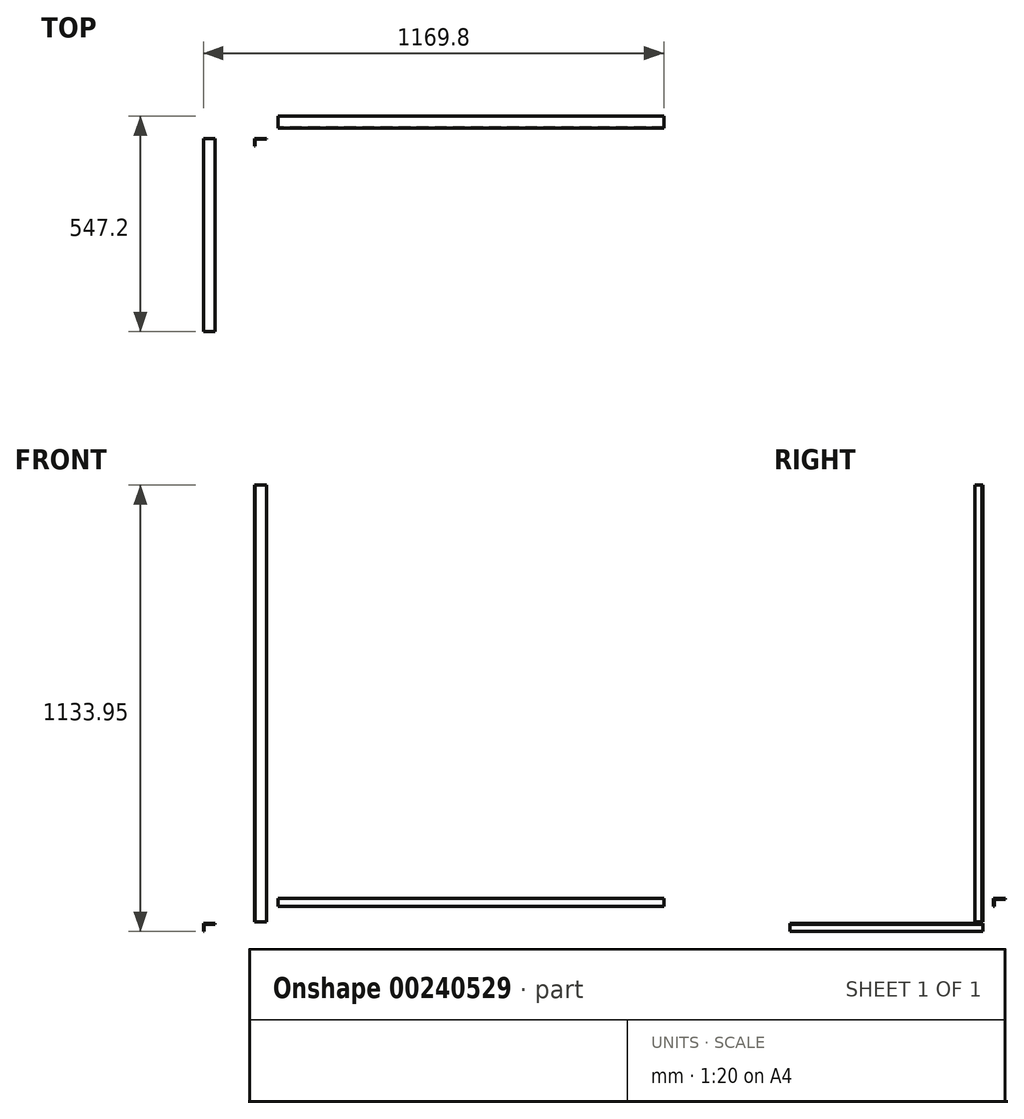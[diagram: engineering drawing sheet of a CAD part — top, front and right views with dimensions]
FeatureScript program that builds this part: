
annotation { "Feature Type Name" : "Feature", "Feature Type Description" : "" }
export const myFeature = defineFeature(function(context is Context, id is Id, definition is map)
    precondition{}
    {
        {
            var Q0;
            Q0=qCreatedBy(makeId("Front.planeOp"),FACE);
            var sketch = newSketch(context, id + "F0", { "sketchPlane" : qUnion([Q0])});
            skLineSegment(sketch, "E0", {"start": v(-189.8, -23.95) * mm, "end": v(-189.8, -3.95) * mm});
            skLineSegment(sketch, "E1", {"start": v(-189.8, -3.95) * mm, "end": v(-159.8, -3.95) * mm});
            skLineSegment(sketch, "E2.0", {"start": v(-187.8, -23.95) * mm, "end": v(-187.8, -5.95) * mm});
            skLineSegment(sketch, "E3.0", {"start": v(-187.8, -5.95) * mm, "end": v(-159.8, -5.95) * mm});
            skLineSegment(sketch, "E4", {"start": v(-159.8, -3.95) * mm, "end": v(-159.8, -5.95) * mm});
            skLineSegment(sketch, "E5", {"start": v(-189.8, -23.95) * mm, "end": v(-187.8, -23.95) * mm});
            skSolve(sketch);
        }
        {
            var Q0;
            Q0=qCreatedBy(makeId("Right.planeOp"),FACE);
            var sketch = newSketch(context, id + "F1", { "sketchPlane" : qUnion([Q0])});
            skLineSegment(sketch, "E6", {"start": v(27.2, 39.41) * mm, "end": v(27.2, 59.41) * mm});
            skLineSegment(sketch, "E7", {"start": v(27.2, 59.41) * mm, "end": v(57.2, 59.41) * mm});
            skLineSegment(sketch, "E8.0", {"start": v(29.2, 39.41) * mm, "end": v(29.2, 57.41) * mm});
            skLineSegment(sketch, "E9.0", {"start": v(29.2, 57.41) * mm, "end": v(57.2, 57.41) * mm});
            skLineSegment(sketch, "E10", {"start": v(57.2, 59.41) * mm, "end": v(57.2, 57.41) * mm});
            skLineSegment(sketch, "E11", {"start": v(27.2, 39.41) * mm, "end": v(29.2, 39.41) * mm});
            skSolve(sketch);
        }
        {
            var Q0;
            Q0=qCreatedBy(makeId("Top.planeOp"),FACE);
            var sketch = newSketch(context, id + "F2", { "sketchPlane" : qUnion([Q0])});
            skLineSegment(sketch, "E12", {"start": v(-60, -19.46) * mm, "end": v(-60, 0.54) * mm});
            skLineSegment(sketch, "E13", {"start": v(-60, 0.54) * mm, "end": v(-30, 0.54) * mm});
            skLineSegment(sketch, "E14.0", {"start": v(-58, -19.46) * mm, "end": v(-58, -1.46) * mm});
            skLineSegment(sketch, "E15.0", {"start": v(-58, -1.46) * mm, "end": v(-30, -1.46) * mm});
            skLineSegment(sketch, "E16", {"start": v(-30, 0.54) * mm, "end": v(-30, -1.46) * mm});
            skLineSegment(sketch, "E17", {"start": v(-60, -19.46) * mm, "end": v(-58, -19.46) * mm});
            skSolve(sketch);
        }
        {
            var Q0;
            Q0=makeQuery(id+"F0.imprint","IMPRINT",FACE,{"disambiguationData":[TD([[makeQuery(id+"F0.imprint","IMPRINT",EDGE,{"derivedFrom":sQuery(id+"F0.wireOp",EDGE,"E0")}),-1.0]])]});
            extrude(context, id + "F3", {"entities" : qUnion([Q0]), "depth" : 490 * mm});
        }
        {
            var Q0;
            Q0=makeQuery(id+"F1.imprint","IMPRINT",FACE,{"disambiguationData":[TD([[makeQuery(id+"F1.imprint","IMPRINT",EDGE,{"derivedFrom":sQuery(id+"F1.wireOp",EDGE,"E6")}),-1.0]])]});
            extrude(context, id + "F4", {"entities" : qUnion([Q0]), "depth" : 980 * mm});
        }
        {
            var Q0;
            Q0=makeQuery(id+"F2.imprint","IMPRINT",FACE,{"disambiguationData":[TD([[makeQuery(id+"F2.imprint","IMPRINT",EDGE,{"derivedFrom":sQuery(id+"F2.wireOp",EDGE,"E12")}),-1.0]])]});
            extrude(context, id + "F5", {"entities" : qUnion([Q0]), "depth" : 1110 * mm});
        }
    });
